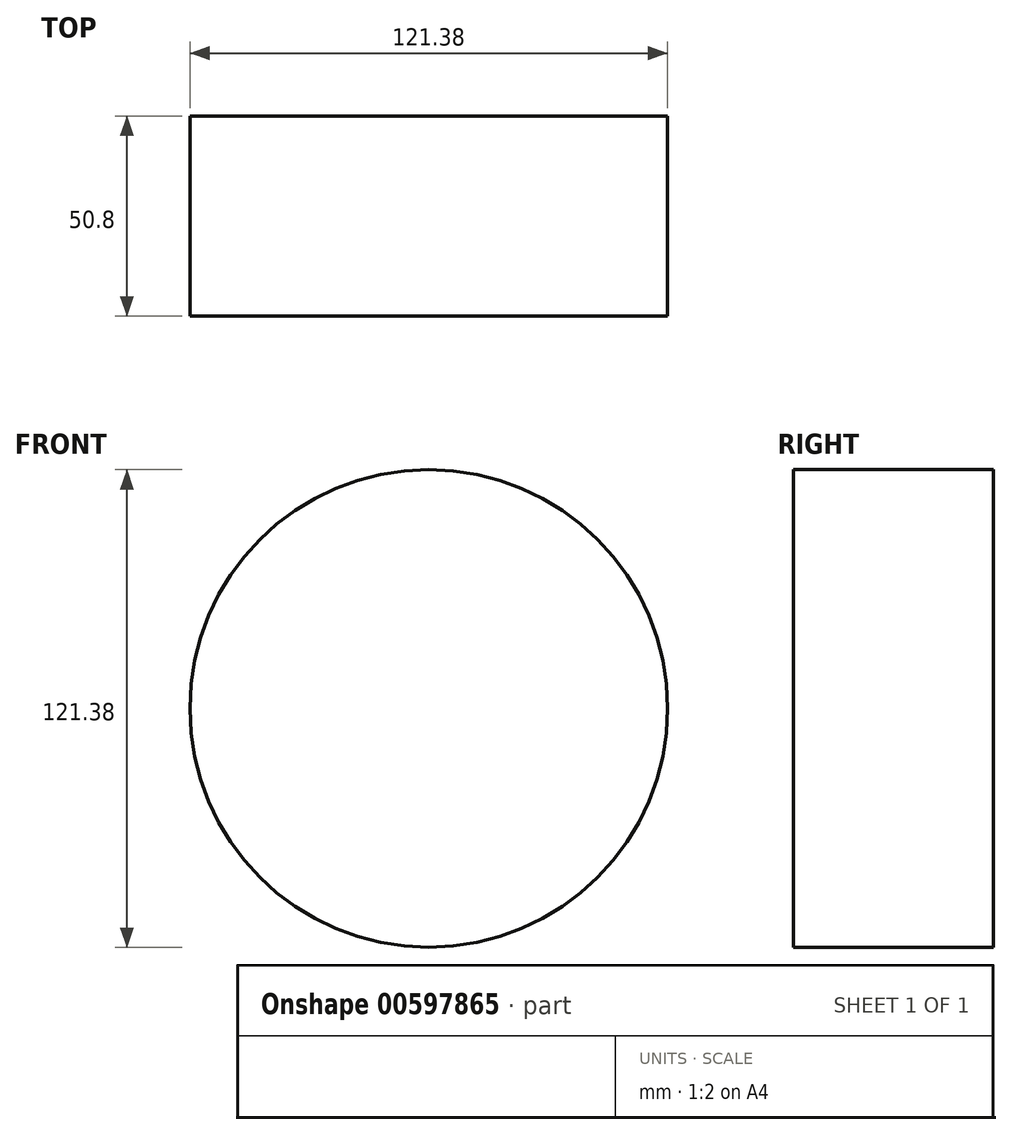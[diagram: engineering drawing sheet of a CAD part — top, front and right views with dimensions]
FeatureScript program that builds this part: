
annotation { "Feature Type Name" : "Feature", "Feature Type Description" : "" }
export const myFeature = defineFeature(function(context is Context, id is Id, definition is map)
    precondition{}
    {
        {
            var Q0;
            Q0=qCreatedBy(makeId("Front.planeOp"),FACE);
            var sketch = newSketch(context, id + "F0", { "sketchPlane" : qUnion([Q0])});
            skCircle(sketch, "E0", {"center": v(0, 0) * mm, "radius": 60.7 * mm});
            skSolve(sketch);
        }
        {
            var Q0;
            Q0=makeQuery(id+"F0.imprint","IMPRINT",FACE,{"disambiguationData":[TD([[makeQuery(id+"F0.imprint","IMPRINT",EDGE,{"derivedFrom":sQuery(id+"F0.wireOp",EDGE,"E0")}),1.0]])]});
            extrude(context, id + "F1", {"entities" : qUnion([Q0]), "depth" : 50.8 * mm, "offsetDistance" : 25.4 * mm});
        }
        {
            var Q0;
            Q0=makeQuery(id+"F1.opExtrude","CAP_FACE",FACE,{"disambiguationData":[OSD([sQuery(id+"F0.wireOp",EDGE,"E0")])],"isStart":false});
            var sketch = newSketch(context, id + "F2", { "sketchPlane" : qUnion([Q0])});
            skSolve(sketch);
        }
        {
            var Q0;
            Q0=makeQuery(id+"F2.imprint","IMPRINT",FACE,{"disambiguationData":[TD([[makeQuery(id+"F2.imprint","IMPRINT",EDGE,{"derivedFrom":makeQuery(id+"F1.opExtrude","CAP_EDGE",EDGE,{"disambiguationData":[OSD([sQuery(id+"F0.wireOp",EDGE,"E0")])],"isStart":false})}),1.0]])]});
            var sketch = newSketch(context, id + "F3", { "sketchPlane" : qUnion([Q0])});
            skLineSegment(sketch, "E1.bottom", {"start": v(0, 35.4) * mm, "end": v(55.1, 35.4) * mm});
            skLineSegment(sketch, "E1.top", {"start": v(0, -24.82) * mm, "end": v(55.1, -24.82) * mm});
            skLineSegment(sketch, "E1.left", {"start": v(0, 35.4) * mm, "end": v(0, -24.82) * mm});
            skLineSegment(sketch, "E1.right", {"start": v(55.1, 35.4) * mm, "end": v(55.1, -24.82) * mm});
            skSolve(sketch);
        }
        {
            var Q0;
            Q0=sQuery(id+"F3.wireOp",EDGE,"E1.top");
            var Q1;
            Q1=sQuery(id+"F3.wireOp",EDGE,"E1.left");
            var Q2;
            Q2=sQuery(id+"F3.wireOp",EDGE,"E1.bottom");
            var Q3;
            Q3=sQuery(id+"F3.wireOp",EDGE,"E1.right");
            extrude(context, id + "F4", {"bodyType" : ToolBodyType.SURFACE, "surfaceEntities" : qUnion([Q0, Q1, Q2, Q3]), "depth" : 76.2 * mm, "offsetDistance" : 25.4 * mm});
        }
    });
